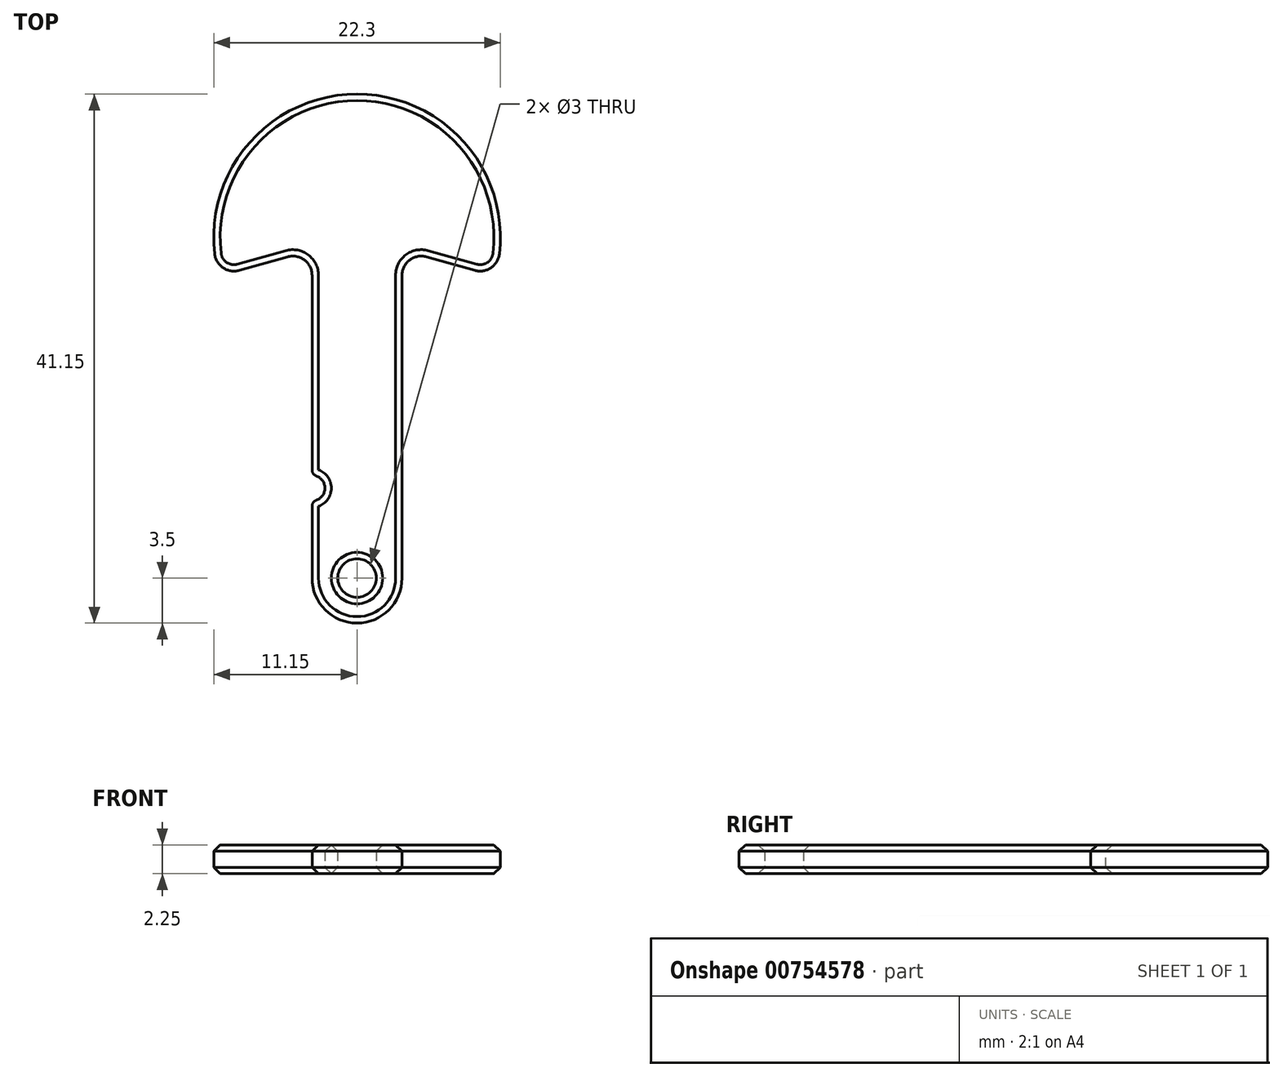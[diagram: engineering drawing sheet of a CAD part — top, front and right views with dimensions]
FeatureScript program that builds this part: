
annotation { "Feature Type Name" : "Feature", "Feature Type Description" : "" }
export const myFeature = defineFeature(function(context is Context, id is Id, definition is map)
    precondition{}
    {
        {
            var Q0;
            Q0=qCreatedBy(makeId("Top.planeOp"),FACE);
            var sketch = newSketch(context, id + "F0", { "sketchPlane" : qUnion([Q0])});
            skArc(sketch, "E0", {"start": v(10.74, -3) * mm, "mid": v(0, 11.15) * mm, "end": v(-10.74, -3) * mm});
            skLineSegment(sketch, "E1.top", {"start": v(0, -30) * mm, "end": v(0, -30) * mm});
            skLineSegment(sketch, "E1.left", {"start": v(-3.5, -0.98) * mm, "end": v(-3.5, -18.09) * mm});
            skLineSegment(sketch, "E1.right", {"start": v(3.5, 0) * mm, "end": v(3.5, -26.5) * mm});
            skLineSegment(sketch, "E2", {"start": v(-7.73, -3) * mm, "end": v(7.83, -3) * mm, "construction": true});
            skLineSegment(sketch, "E3", {"start": v(7.83, -3) * mm, "end": v(15.22, -3) * mm});
            skLineSegment(sketch, "E4", {"start": v(-7.73, -3) * mm, "end": v(-15.27, -3) * mm});
            skLineSegment(sketch, "E5", {"start": v(-10.74, -3) * mm, "end": v(-3.5, -0.98) * mm});
            skLineSegment(sketch, "E6", {"start": v(10.74, -3) * mm, "end": v(3.5, -0.98) * mm});
            skPoint(sketch, "E7.visualSharp", {"position": v(-3.5, -30) * mm});
            skArc(sketch, "E7.filletArc", {"start": v(-3.5, -26.5) * mm, "mid": v(-2.47, -28.97) * mm, "end": v(0, -30) * mm});
            skPoint(sketch, "E8.visualSharp", {"position": v(3.5, -30) * mm});
            skArc(sketch, "E8.filletArc", {"start": v(0, -30) * mm, "mid": v(2.47, -28.97) * mm, "end": v(3.5, -26.5) * mm});
            skCircle(sketch, "E9", {"center": v(0, -26.5) * mm, "radius": 1.5 * mm});
            skArc(sketch, "E10", {"start": v(-3.17, -20.44) * mm, "mid": v(-2.5, -19.5) * mm, "end": v(-3.17, -18.56) * mm});
            skLineSegment(sketch, "E11.trimOffspring", {"start": v(-3.5, -20.91) * mm, "end": v(-3.5, -26.5) * mm});
            skPoint(sketch, "E12.visualSharp", {"position": v(-3.5, -20.5) * mm});
            skArc(sketch, "E12.filletArc", {"start": v(-3.17, -20.44) * mm, "mid": v(-3.4, -20.63) * mm, "end": v(-3.5, -20.91) * mm});
            skPoint(sketch, "E13.visualSharp", {"position": v(-3.5, -18.5) * mm});
            skArc(sketch, "E13.filletArc", {"start": v(-3.5, -18.09) * mm, "mid": v(-3.4, -18.37) * mm, "end": v(-3.17, -18.56) * mm});
            skSolve(sketch);
        }
        {
            var Q0;
            Q0=makeQuery(id+"F0.imprint","IMPRINT",FACE,{"disambiguationData":[TD([[makeQuery(id+"F0.imprint","IMPRINT",EDGE,{"derivedFrom":sQuery(id+"F0.wireOp",EDGE,"E0")}),1.0]])]});
            extrude(context, id + "F1", {"entities" : qUnion([Q0]), "depth" : 2.25 * mm, "offsetDistance" : 25 * mm});
        }
        {
            var Q0;
            Q0=makeQuery(id+"F1.opExtrude","SWEPT_EDGE",EDGE,{"disambiguationData":[OSD([sQuery(id+"F0.wireOp",EDGE,"E0"),sQuery(id+"F0.wireOp",EDGE,"E6")])]});
            var Q1;
            Q1=makeQuery(id+"F1.opExtrude","SWEPT_EDGE",EDGE,{"disambiguationData":[OSD([sQuery(id+"F0.wireOp",EDGE,"E0"),sQuery(id+"F0.wireOp",EDGE,"E5")])]});
            var Q2;
            Q2=makeQuery(id+"F1.opExtrude","SWEPT_EDGE",EDGE,{"disambiguationData":[OSD([sQuery(id+"F0.wireOp",EDGE,"E1.left"),sQuery(id+"F0.wireOp",EDGE,"E5")])]});
            var Q3;
            Q3=makeQuery(id+"F1.opExtrude","SWEPT_EDGE",EDGE,{"disambiguationData":[OSD([sQuery(id+"F0.wireOp",EDGE,"E1.right"),sQuery(id+"F0.wireOp",EDGE,"E6")])]});
            fillet(context, id + "F2", {"entities" : qUnion([Q0, Q1, Q2, Q3]), "radius" : 1.5 * mm, "tangentPropagation" : true, "allowEdgeOverflow" : false});
        }
        {
            var Q0;
            Q0=makeQuery(id+"F1.opExtrude","CAP_FACE",FACE,{"disambiguationData":[OSD([sQuery(id+"F0.wireOp",EDGE,"E0"),sQuery(id+"F0.wireOp",EDGE,"E1.left"),sQuery(id+"F0.wireOp",EDGE,"E1.right"),sQuery(id+"F0.wireOp",EDGE,"E5"),sQuery(id+"F0.wireOp",EDGE,"E6"),sQuery(id+"F0.wireOp",EDGE,"E7.filletArc"),sQuery(id+"F0.wireOp",EDGE,"E8.filletArc"),sQuery(id+"F0.wireOp",EDGE,"E9")])],"isStart":false});
            var Q1;
            Q1=makeQuery(id+"F1.opExtrude","CAP_FACE",FACE,{"disambiguationData":[OSD([sQuery(id+"F0.wireOp",EDGE,"E0"),sQuery(id+"F0.wireOp",EDGE,"E1.left"),sQuery(id+"F0.wireOp",EDGE,"E1.right"),sQuery(id+"F0.wireOp",EDGE,"E5"),sQuery(id+"F0.wireOp",EDGE,"E6"),sQuery(id+"F0.wireOp",EDGE,"E7.filletArc"),sQuery(id+"F0.wireOp",EDGE,"E8.filletArc"),sQuery(id+"F0.wireOp",EDGE,"E9")])],"isStart":true});
            chamfer(context, id + "F3", {"entities" : qUnion([Q0, Q1]), "width" : 0.5 * mm, "tangentPropagation" : true});
        }
    });
